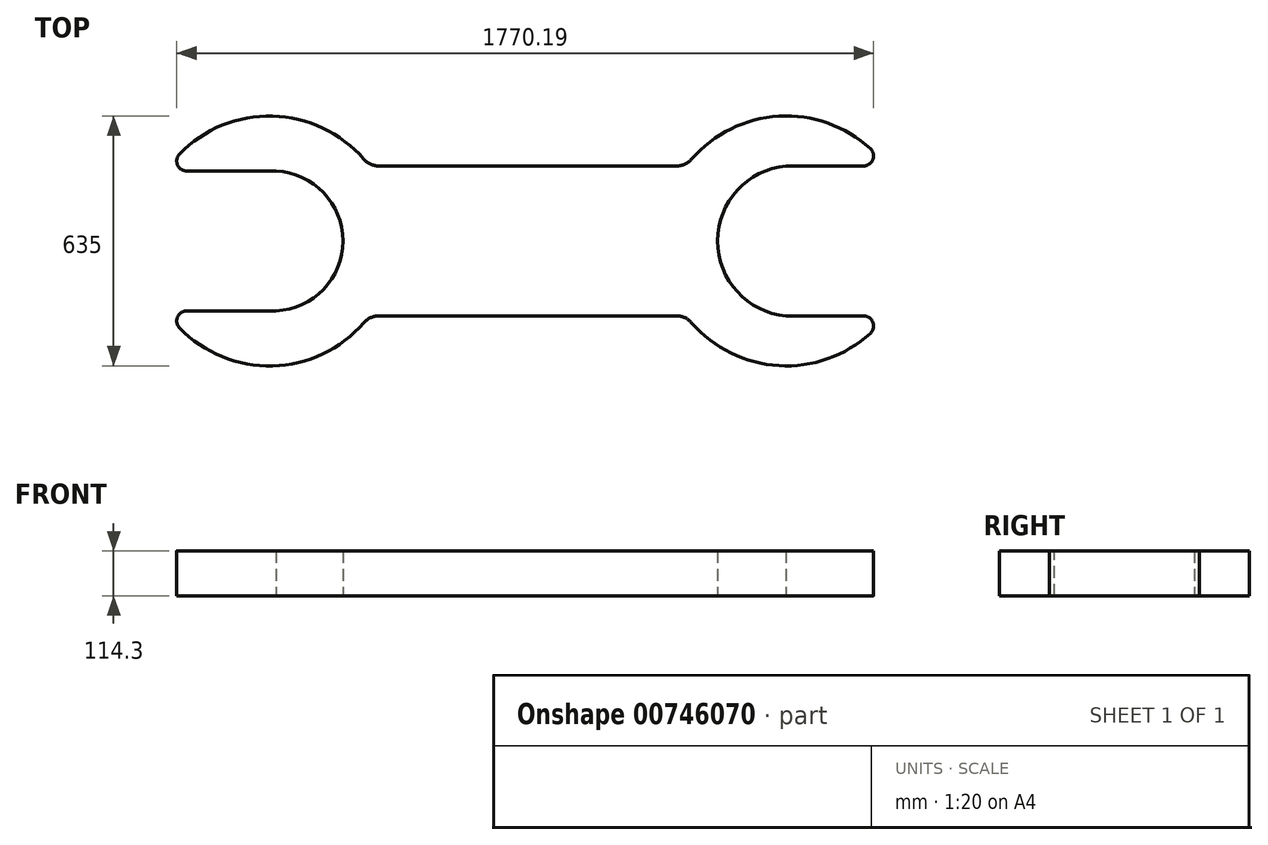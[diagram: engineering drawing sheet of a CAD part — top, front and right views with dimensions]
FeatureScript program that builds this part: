
annotation { "Feature Type Name" : "Feature", "Feature Type Description" : "" }
export const myFeature = defineFeature(function(context is Context, id is Id, definition is map)
    precondition{}
    {
        {
            var Q0;
            Q0=qCreatedBy(makeId("Top.planeOp"),FACE);
            var sketch = newSketch(context, id + "F0", { "sketchPlane" : qUnion([Q0])});
            skArc(sketch, "E0", {"start": v(-305.85, -177.8) * mm, "mid": v(-50.6, -317.4) * mm, "end": v(211.2, -190.5) * mm});
            skArc(sketch, "E1", {"start": v(1524, 190.5) * mm, "mid": v(1270, 317.5) * mm, "end": v(1016, 190.5) * mm});
            skLineSegment(sketch, "E2.0", {"start": v(-305.85, -177.8) * mm, "end": v(-25.54, -177.8) * mm});
            skLineSegment(sketch, "E3.0", {"start": v(-305.85, 177.8) * mm, "end": v(-25.54, 177.8) * mm});
            skLineSegment(sketch, "E4.0", {"start": v(211.2, 190.5) * mm, "end": v(1016, 190.5) * mm});
            skLineSegment(sketch, "E5.0", {"start": v(211.2, -190.5) * mm, "end": v(1016, -190.5) * mm});
            skArc(sketch, "E6", {"start": v(-42.8, -177.8) * mm, "mid": v(143.84, 0) * mm, "end": v(-42.8, 177.8) * mm});
            skArc(sketch, "E7", {"start": v(1270, 190.5) * mm, "mid": v(1096.12, 0) * mm, "end": v(1270, -190.5) * mm});
            skLineSegment(sketch, "E8.trimOffspring", {"start": v(1270, 190.5) * mm, "end": v(1524, 190.5) * mm});
            skArc(sketch, "E9.trimOffspring", {"start": v(211.2, 190.5) * mm, "mid": v(-50.6, 317.4) * mm, "end": v(-305.85, 177.8) * mm});
            skArc(sketch, "E10.trimOffspring", {"start": v(1016, -190.5) * mm, "mid": v(1270, -317.5) * mm, "end": v(1524, -190.5) * mm});
            skLineSegment(sketch, "E11.trimOffspring", {"start": v(1270, -190.5) * mm, "end": v(1524, -190.5) * mm});
            skSolve(sketch);
        }
        {
            var Q0;
            Q0 = qSketchRegion(id + "F0", true);
            extrude(context, id + "F1", {"entities" : qUnion([Q0]), "depth" : 114.3 * mm, "offsetDistance" : 25.4 * mm});
        }
        {
            var Q0;
            Q0=makeQuery(id+"F1.opExtrude","SWEPT_EDGE",EDGE,{"disambiguationData":[OSD([sQuery(id+"F0.wireOp",EDGE,"E4.0"),sQuery(id+"F0.wireOp",EDGE,"E9.trimOffspring")])]});
            var Q1;
            Q1=makeQuery(id+"F1.opExtrude","SWEPT_EDGE",EDGE,{"disambiguationData":[OSD([sQuery(id+"F0.wireOp",EDGE,"E1"),sQuery(id+"F0.wireOp",EDGE,"E4.0")])]});
            var Q2;
            Q2=makeQuery(id+"F1.opExtrude","SWEPT_EDGE",EDGE,{"disambiguationData":[OSD([sQuery(id+"F0.wireOp",EDGE,"E0"),sQuery(id+"F0.wireOp",EDGE,"E5.0")])]});
            var Q3;
            Q3=makeQuery(id+"F1.opExtrude","SWEPT_EDGE",EDGE,{"disambiguationData":[OSD([sQuery(id+"F0.wireOp",EDGE,"E5.0"),sQuery(id+"F0.wireOp",EDGE,"E10.trimOffspring")])]});
            fillet(context, id + "F2", {"entities" : qUnion([Q0, Q1, Q2, Q3]), "radius" : 50.8 * mm, "tangentPropagation" : true, "allowEdgeOverflow" : false});
        }
        {
            var Q0;
            Q0=makeQuery(id+"F1.opExtrude","SWEPT_EDGE",EDGE,{"disambiguationData":[OSD([sQuery(id+"F0.wireOp",EDGE,"E3.0"),sQuery(id+"F0.wireOp",EDGE,"E9.trimOffspring")])]});
            var Q1;
            Q1=makeQuery(id+"F1.opExtrude","SWEPT_EDGE",EDGE,{"disambiguationData":[OSD([sQuery(id+"F0.wireOp",EDGE,"E0"),sQuery(id+"F0.wireOp",EDGE,"E2.0")])]});
            var Q2;
            Q2=makeQuery(id+"F1.opExtrude","SWEPT_EDGE",EDGE,{"disambiguationData":[OSD([sQuery(id+"F0.wireOp",EDGE,"E1"),sQuery(id+"F0.wireOp",EDGE,"E8.trimOffspring")])]});
            var Q3;
            Q3=makeQuery(id+"F1.opExtrude","SWEPT_EDGE",EDGE,{"disambiguationData":[OSD([sQuery(id+"F0.wireOp",EDGE,"E10.trimOffspring"),sQuery(id+"F0.wireOp",EDGE,"E11.trimOffspring")])]});
            fillet(context, id + "F3", {"entities" : qUnion([Q0, Q1, Q2, Q3]), "radius" : 25.4 * mm, "tangentPropagation" : true, "allowEdgeOverflow" : false});
        }
    });
